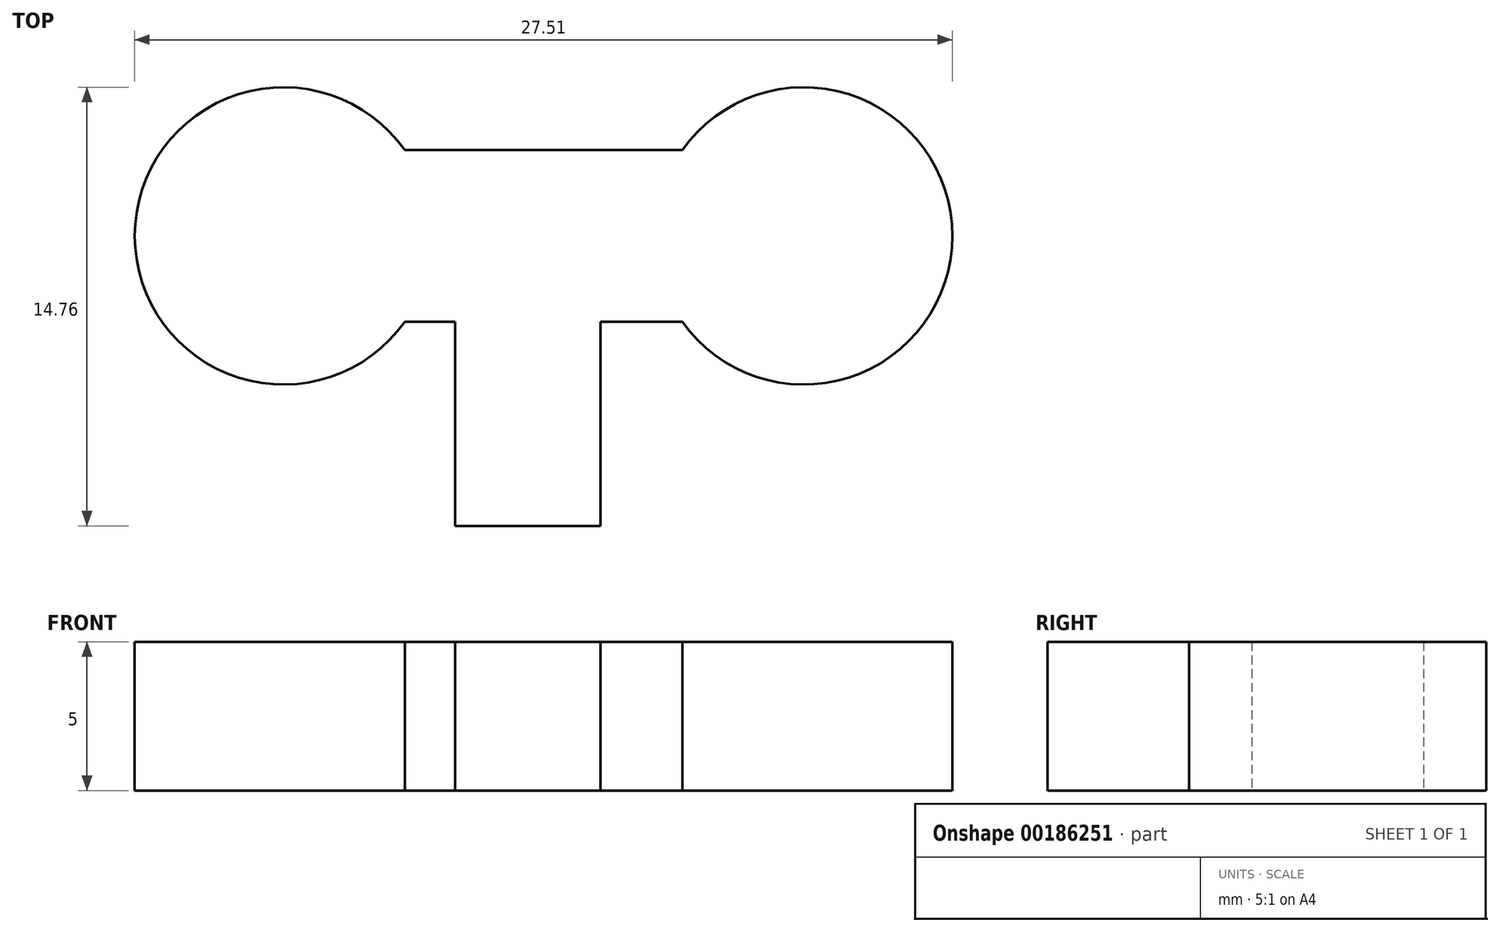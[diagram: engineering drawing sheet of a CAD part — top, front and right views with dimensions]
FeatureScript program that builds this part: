
annotation { "Feature Type Name" : "Feature", "Feature Type Description" : "" }
export const myFeature = defineFeature(function(context is Context, id is Id, definition is map)
    precondition{}
    {
        {
            var Q0;
            Q0=qCreatedBy(makeId("Top.planeOp"),FACE);
            var sketch = newSketch(context, id + "F0", { "sketchPlane" : qUnion([Q0])});
            skLineSegment(sketch, "E0.bottom", {"start": v(-3.45, 17.53) * mm, "end": v(5.88, 17.53) * mm});
            skLineSegment(sketch, "E0.top", {"start": v(-3.45, 23.3) * mm, "end": v(5.88, 23.3) * mm});
            skLineSegment(sketch, "E0.left", {"start": v(-3.45, 17.53) * mm, "end": v(-3.45, 23.3) * mm});
            skLineSegment(sketch, "E0.right", {"start": v(5.88, 17.53) * mm, "end": v(5.88, 23.3) * mm});
            skLineSegment(sketch, "E1.bottom", {"start": v(-1.75, 17.53) * mm, "end": v(3.13, 17.53) * mm});
            skLineSegment(sketch, "E1.top", {"start": v(-1.75, 10.66) * mm, "end": v(3.13, 10.66) * mm});
            skLineSegment(sketch, "E1.left", {"start": v(-1.75, 17.53) * mm, "end": v(-1.75, 10.66) * mm});
            skLineSegment(sketch, "E1.right", {"start": v(3.13, 17.53) * mm, "end": v(3.13, 10.66) * mm});
            skArc(sketch, "E2", {"start": v(5.88, 17.53) * mm, "mid": v(14.97, 20.42) * mm, "end": v(5.88, 23.3) * mm});
            skArc(sketch, "E3", {"start": v(-3.45, 23.3) * mm, "mid": v(-12.54, 20.42) * mm, "end": v(-3.45, 17.53) * mm});
            skSolve(sketch);
        }
        {
            var Q0;
            Q0 = qSketchRegion(id + "F0", true);
            extrude(context, id + "F1", {"entities" : qUnion([Q0]), "depth" : 5 * mm});
        }
    });
